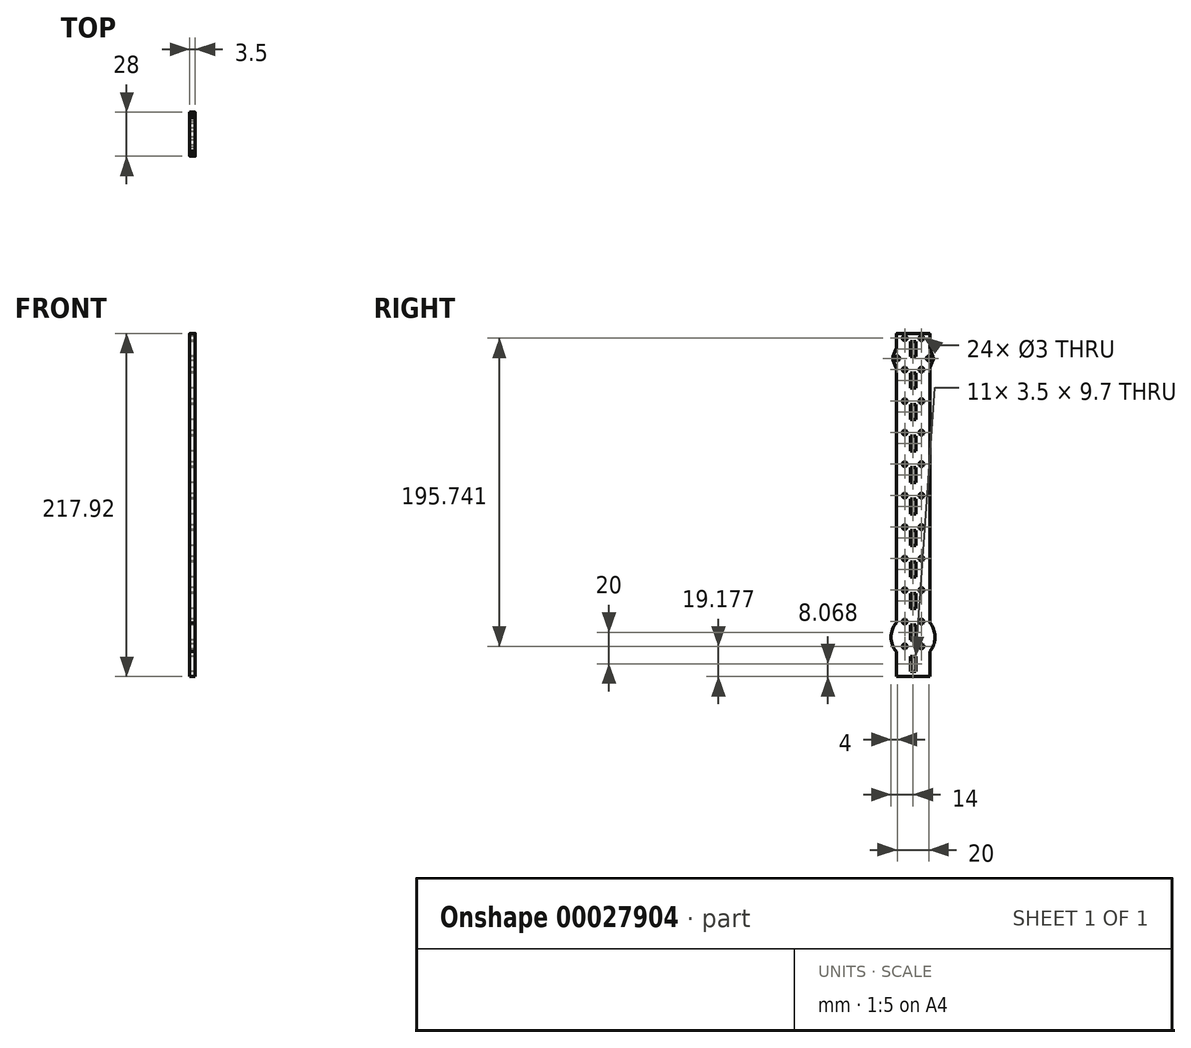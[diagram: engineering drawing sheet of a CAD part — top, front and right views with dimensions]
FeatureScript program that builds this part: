
annotation { "Feature Type Name" : "Feature", "Feature Type Description" : "" }
export const myFeature = defineFeature(function(context is Context, id is Id, definition is map)
    precondition{}
    {
        {
            var Q0;
            Q0=qCreatedBy(makeId("Right.planeOp"),FACE);
            var sketch = newSketch(context, id + "F0", { "sketchPlane" : qUnion([Q0])});
            skLineSegment(sketch, "E0.rect.top", {"start": v(10.14, 107.96) * mm, "end": v(-10.14, 107.96) * mm});
            skLineSegment(sketch, "E0.rect.left", {"start": v(10.64, -107.46) * mm, "end": v(10.64, -94.07) * mm});
            skLineSegment(sketch, "E0.rect.right", {"start": v(-10.64, -107.46) * mm, "end": v(-10.64, -94.07) * mm});
            skPoint(sketch, "E0.rect.middle", {"position": v(0, 0) * mm});
            skLineSegment(sketch, "E1", {"start": v(-10.64, 83.44) * mm, "end": v(10.64, 83.44) * mm, "construction": true});
            skLineSegment(sketch, "E2", {"start": v(10.64, 83.44) * mm, "end": v(0, 107.96) * mm, "construction": true});
            skLineSegment(sketch, "E3", {"start": v(0, 107.96) * mm, "end": v(0, -80.34) * mm, "construction": true});
            skLineSegment(sketch, "E4.rect.bottom", {"start": v(1.75, 93.26) * mm, "end": v(-1.75, 93.26) * mm});
            skLineSegment(sketch, "E4.rect.top", {"start": v(1.75, 102.96) * mm, "end": v(-1.75, 102.96) * mm});
            skLineSegment(sketch, "E4.rect.left", {"start": v(1.75, 93.26) * mm, "end": v(1.75, 102.96) * mm});
            skLineSegment(sketch, "E4.rect.right", {"start": v(-1.75, 93.26) * mm, "end": v(-1.75, 102.96) * mm});
            skPoint(sketch, "E4.rect.middle", {"position": v(0, 98.1) * mm});
            skCircle(sketch, "E5", {"center": v(-5.32, 104.96) * mm, "radius": 1.5 * mm});
            skCircle(sketch, "E6.MirrorC", {"center": v(5.32, 104.96) * mm, "radius": 1.5 * mm});
            skCircle(sketch, "E7.0.1.0", {"center": v(-5.32, 84.96) * mm, "radius": 1.5 * mm});
            skCircle(sketch, "E7.0.1.1", {"center": v(5.32, 84.96) * mm, "radius": 1.5 * mm});
            skLineSegment(sketch, "E7.0.1.2", {"start": v(1.75, 73.26) * mm, "end": v(1.75, 82.96) * mm});
            skLineSegment(sketch, "E7.0.1.3", {"start": v(1.75, 82.96) * mm, "end": v(-1.75, 82.96) * mm});
            skLineSegment(sketch, "E7.0.1.4", {"start": v(-1.75, 73.26) * mm, "end": v(-1.75, 82.96) * mm});
            skLineSegment(sketch, "E7.0.1.5", {"start": v(1.75, 73.26) * mm, "end": v(-1.75, 73.26) * mm});
            skCircle(sketch, "E7.0.2.0", {"center": v(-5.32, 64.96) * mm, "radius": 1.5 * mm});
            skCircle(sketch, "E7.0.2.1", {"center": v(5.32, 64.96) * mm, "radius": 1.5 * mm});
            skLineSegment(sketch, "E7.0.2.2", {"start": v(1.75, 53.26) * mm, "end": v(1.75, 62.96) * mm});
            skLineSegment(sketch, "E7.0.2.3", {"start": v(1.75, 62.96) * mm, "end": v(-1.75, 62.96) * mm});
            skLineSegment(sketch, "E7.0.2.4", {"start": v(-1.75, 53.26) * mm, "end": v(-1.75, 62.96) * mm});
            skLineSegment(sketch, "E7.0.2.5", {"start": v(1.75, 53.26) * mm, "end": v(-1.75, 53.26) * mm});
            skCircle(sketch, "E7.0.3.0", {"center": v(-5.32, 44.96) * mm, "radius": 1.5 * mm});
            skCircle(sketch, "E7.0.3.1", {"center": v(5.32, 44.96) * mm, "radius": 1.5 * mm});
            skLineSegment(sketch, "E7.0.3.2", {"start": v(1.75, 33.26) * mm, "end": v(1.75, 42.96) * mm});
            skLineSegment(sketch, "E7.0.3.3", {"start": v(1.75, 42.96) * mm, "end": v(-1.75, 42.96) * mm});
            skLineSegment(sketch, "E7.0.3.4", {"start": v(-1.75, 33.26) * mm, "end": v(-1.75, 42.96) * mm});
            skLineSegment(sketch, "E7.0.3.5", {"start": v(1.75, 33.26) * mm, "end": v(-1.75, 33.26) * mm});
            skCircle(sketch, "E7.0.4.0", {"center": v(-5.32, 24.96) * mm, "radius": 1.5 * mm});
            skCircle(sketch, "E7.0.4.1", {"center": v(5.32, 24.96) * mm, "radius": 1.5 * mm});
            skLineSegment(sketch, "E7.0.4.2", {"start": v(1.75, 13.26) * mm, "end": v(1.75, 22.96) * mm});
            skLineSegment(sketch, "E7.0.4.3", {"start": v(1.75, 22.96) * mm, "end": v(-1.75, 22.96) * mm});
            skLineSegment(sketch, "E7.0.4.4", {"start": v(-1.75, 13.26) * mm, "end": v(-1.75, 22.96) * mm});
            skLineSegment(sketch, "E7.0.4.5", {"start": v(1.75, 13.26) * mm, "end": v(-1.75, 13.26) * mm});
            skCircle(sketch, "E7.0.5.0", {"center": v(-5.32, 4.96) * mm, "radius": 1.5 * mm});
            skCircle(sketch, "E7.0.5.1", {"center": v(5.32, 4.96) * mm, "radius": 1.5 * mm});
            skLineSegment(sketch, "E7.0.5.2", {"start": v(1.75, -6.74) * mm, "end": v(1.75, 2.96) * mm});
            skLineSegment(sketch, "E7.0.5.3", {"start": v(1.75, 2.96) * mm, "end": v(-1.75, 2.96) * mm});
            skLineSegment(sketch, "E7.0.5.4", {"start": v(-1.75, -6.74) * mm, "end": v(-1.75, 2.96) * mm});
            skLineSegment(sketch, "E7.0.5.5", {"start": v(1.75, -6.74) * mm, "end": v(-1.75, -6.74) * mm});
            skCircle(sketch, "E7.0.6.0", {"center": v(-5.32, -15.04) * mm, "radius": 1.5 * mm});
            skCircle(sketch, "E7.0.6.1", {"center": v(5.32, -15.04) * mm, "radius": 1.5 * mm});
            skLineSegment(sketch, "E7.0.6.2", {"start": v(1.75, -26.74) * mm, "end": v(1.75, -17.04) * mm});
            skLineSegment(sketch, "E7.0.6.3", {"start": v(1.75, -17.04) * mm, "end": v(-1.75, -17.04) * mm});
            skLineSegment(sketch, "E7.0.6.4", {"start": v(-1.75, -26.74) * mm, "end": v(-1.75, -17.04) * mm});
            skLineSegment(sketch, "E7.0.6.5", {"start": v(1.75, -26.74) * mm, "end": v(-1.75, -26.74) * mm});
            skCircle(sketch, "E7.0.7.0", {"center": v(-5.32, -35.04) * mm, "radius": 1.5 * mm});
            skCircle(sketch, "E7.0.7.1", {"center": v(5.32, -35.04) * mm, "radius": 1.5 * mm});
            skLineSegment(sketch, "E7.0.7.2", {"start": v(1.75, -46.74) * mm, "end": v(1.75, -37.04) * mm});
            skLineSegment(sketch, "E7.0.7.3", {"start": v(1.75, -37.04) * mm, "end": v(-1.75, -37.04) * mm});
            skLineSegment(sketch, "E7.0.7.4", {"start": v(-1.75, -46.74) * mm, "end": v(-1.75, -37.04) * mm});
            skLineSegment(sketch, "E7.0.7.5", {"start": v(1.75, -46.74) * mm, "end": v(-1.75, -46.74) * mm});
            skCircle(sketch, "E7.0.8.0", {"center": v(-5.32, -55.04) * mm, "radius": 1.5 * mm});
            skCircle(sketch, "E7.0.8.1", {"center": v(5.32, -55.04) * mm, "radius": 1.5 * mm});
            skLineSegment(sketch, "E7.0.8.2", {"start": v(1.75, -66.74) * mm, "end": v(1.75, -57.04) * mm});
            skLineSegment(sketch, "E7.0.8.3", {"start": v(1.75, -57.04) * mm, "end": v(-1.75, -57.04) * mm});
            skLineSegment(sketch, "E7.0.8.4", {"start": v(-1.75, -66.74) * mm, "end": v(-1.75, -57.04) * mm});
            skLineSegment(sketch, "E7.0.8.5", {"start": v(1.75, -66.74) * mm, "end": v(-1.75, -66.74) * mm});
            skCircle(sketch, "E7.0.9.0", {"center": v(-5.32, -75.04) * mm, "radius": 1.5 * mm});
            skCircle(sketch, "E7.0.9.1", {"center": v(5.32, -75.04) * mm, "radius": 1.5 * mm});
            skLineSegment(sketch, "E7.0.10.2", {"start": v(1.75, -106.74) * mm, "end": v(1.75, -97.04) * mm});
            skLineSegment(sketch, "E7.0.10.3", {"start": v(1.75, -97.04) * mm, "end": v(-1.75, -97.04) * mm});
            skLineSegment(sketch, "E7.0.10.4", {"start": v(-1.75, -106.74) * mm, "end": v(-1.75, -97.04) * mm});
            skLineSegment(sketch, "E7.0.10.5", {"start": v(1.75, -106.74) * mm, "end": v(-1.75, -106.74) * mm});
            skLineSegment(sketch, "E7.direction1", {"start": v(-5.32, 104.96) * mm, "end": v(19.68, 104.96) * mm, "construction": true});
            skLineSegment(sketch, "E7.direction2", {"start": v(-5.32, 104.96) * mm, "end": v(-5.32, 84.96) * mm, "construction": true});
            skArc(sketch, "E8", {"start": v(-10.64, -75.87) * mm, "mid": v(-14, -84.97) * mm, "end": v(-10.64, -94.07) * mm});
            skLineSegment(sketch, "E9.trimOffspring", {"start": v(-10.64, -75.87) * mm, "end": v(-10.64, 107.46) * mm});
            skArc(sketch, "E10.trimOffspring", {"start": v(10.64, -94.07) * mm, "mid": v(14, -84.97) * mm, "end": v(10.64, -75.87) * mm});
            skLineSegment(sketch, "E11.trimOffspring", {"start": v(10.64, -75.87) * mm, "end": v(10.64, 107.46) * mm});
            skPoint(sketch, "E12.orphan", {"position": v(1.75, -77.04) * mm});
            skPoint(sketch, "E13.visualSharp", {"position": v(-10.64, -107.96) * mm});
            skPoint(sketch, "E14.visualSharp", {"position": v(10.64, -107.96) * mm});
            skPoint(sketch, "E15.visualSharp", {"position": v(-10.64, 107.96) * mm});
            skArc(sketch, "E15.filletArc", {"start": v(-10.14, 107.96) * mm, "mid": v(-10.5, 107.81) * mm, "end": v(-10.64, 107.46) * mm});
            skPoint(sketch, "E16.visualSharp", {"position": v(10.64, 107.96) * mm});
            skArc(sketch, "E16.filletArc", {"start": v(10.64, 107.46) * mm, "mid": v(10.5, 107.81) * mm, "end": v(10.14, 107.96) * mm});
            skLineSegment(sketch, "E17.trimOffspring", {"start": v(0, -84.97) * mm, "end": v(0, -107.96) * mm, "construction": true});
            skLineSegment(sketch, "E18.0.1.0", {"start": v(1.75, -86.74) * mm, "end": v(1.75, -77.04) * mm});
            skLineSegment(sketch, "E18.0.1.1", {"start": v(1.75, -86.74) * mm, "end": v(-1.75, -86.74) * mm});
            skLineSegment(sketch, "E18.0.1.2", {"start": v(-1.75, -86.74) * mm, "end": v(-1.75, -77.04) * mm});
            skLineSegment(sketch, "E18.0.1.3", {"start": v(1.75, -77.04) * mm, "end": v(-1.75, -77.04) * mm});
            skLineSegment(sketch, "E18.direction1", {"start": v(1.75, -66.74) * mm, "end": v(26.9, -66.74) * mm, "construction": true});
            skLineSegment(sketch, "E18.direction2", {"start": v(1.75, -66.74) * mm, "end": v(1.75, -86.74) * mm, "construction": true});
            skLineSegment(sketch, "E19", {"start": v(-5.32, -35.04) * mm, "end": v(-5.32, -107.96) * mm, "construction": true});
            skLineSegment(sketch, "E20", {"start": v(5.32, -35.04) * mm, "end": v(5.32, -107.96) * mm, "construction": true});
            skCircle(sketch, "E21", {"center": v(5.32, -90.78) * mm, "radius": 1.5 * mm});
            skCircle(sketch, "E22.MirrorC", {"center": v(-5.32, -90.78) * mm, "radius": 1.5 * mm});
            skCircle(sketch, "E23", {"center": v(-10, 92.13) * mm, "radius": 1.5 * mm});
            skCircle(sketch, "E24.MirrorC", {"center": v(10, 92.13) * mm, "radius": 1.5 * mm});
            skLineSegment(sketch, "E25", {"start": v(16.33, 92.13) * mm, "end": v(-13.22, 92.13) * mm, "construction": true});
            skLineSegment(sketch, "E26", {"start": v(-13.22, 92.13) * mm, "end": v(-10.64, 98.45) * mm});
            skLineSegment(sketch, "E27.MirrorCS", {"start": v(-13.22, 92.13) * mm, "end": v(-10.64, 85.81) * mm});
            skLineSegment(sketch, "E28.MirrorCS", {"start": v(13.22, 92.13) * mm, "end": v(10.64, 98.45) * mm});
            skLineSegment(sketch, "E29.MirrorCS", {"start": v(13.22, 92.13) * mm, "end": v(10.64, 85.81) * mm});
            skLineSegment(sketch, "E30.bottom", {"start": v(0, -107.96) * mm, "end": v(10.64, -107.96) * mm});
            skLineSegment(sketch, "E30.top", {"start": v(-10.64, -109.96) * mm, "end": v(10.64, -109.96) * mm});
            skLineSegment(sketch, "E30.left", {"start": v(-10.64, -107.96) * mm, "end": v(-10.64, -109.96) * mm});
            skLineSegment(sketch, "E30.right", {"start": v(10.64, -107.96) * mm, "end": v(10.64, -109.96) * mm});
            skLineSegment(sketch, "E31", {"start": v(10.64, -107.96) * mm, "end": v(10.64, -107.46) * mm});
            skLineSegment(sketch, "E32", {"start": v(-10.64, -107.96) * mm, "end": v(-10.64, -107.46) * mm});
            skSolve(sketch);
        }
        {
            var Q0;
            Q0 = qSketchRegion(id + "F0", true);
            extrude(context, id + "F1", {"entities" : qUnion([Q0]), "depth" : 3.5 * mm});
        }
        {
            var Q0;
            Q0=makeQuery(id+"F1.opExtrude","SWEPT_EDGE",EDGE,{"disambiguationData":[OSD([sQuery(id+"F0.wireOp",EDGE,"E26"),sQuery(id+"F0.wireOp",EDGE,"E27.MirrorCS")])]});
            var Q1;
            Q1=makeQuery(id+"F1.opExtrude","SWEPT_EDGE",EDGE,{"disambiguationData":[OSD([sQuery(id+"F0.wireOp",EDGE,"b3f7ac1b-f8fb-4887-b317-526ebcccde5e"),sQuery(id+"F0.wireOp",EDGE,"81c05ff1-11e3-4124-91b9-50cd6c8fe2a20.MirrorCS")])]});
            var Q2;
            Q2=makeQuery(id+"F1.opExtrude","SWEPT_EDGE",EDGE,{"disambiguationData":[OSD([sQuery(id+"F0.wireOp",EDGE,"E9.trimOffspring"),sQuery(id+"F0.wireOp",EDGE,"E27.MirrorCS")])]});
            var Q3;
            Q3=makeQuery(id+"F1.opExtrude","SWEPT_EDGE",EDGE,{"disambiguationData":[OSD([sQuery(id+"F0.wireOp",EDGE,"E9.trimOffspring"),sQuery(id+"F0.wireOp",EDGE,"E26")])]});
            var Q4;
            Q4=makeQuery(id+"F1.opExtrude","SWEPT_EDGE",EDGE,{"disambiguationData":[OSD([sQuery(id+"F0.wireOp",EDGE,"E11.trimOffspring"),sQuery(id+"F0.wireOp",EDGE,"b3f7ac1b-f8fb-4887-b317-526ebcccde5e")])]});
            var Q5;
            Q5=makeQuery(id+"F1.opExtrude","SWEPT_EDGE",EDGE,{"disambiguationData":[OSD([sQuery(id+"F0.wireOp",EDGE,"E11.trimOffspring"),sQuery(id+"F0.wireOp",EDGE,"81c05ff1-11e3-4124-91b9-50cd6c8fe2a20.MirrorCS")])]});
            var Q6;
            Q6=makeQuery(id+"F1.opExtrude","SWEPT_EDGE",EDGE,{"disambiguationData":[OSD([sQuery(id+"F0.wireOp",EDGE,"E28.MirrorCS"),sQuery(id+"F0.wireOp",EDGE,"E29.MirrorCS")])]});
            fillet(context, id + "F2", {"entities" : qUnion([Q0, Q1, Q2, Q3, Q4, Q5, Q6]), "radius" : 3 * mm, "tangentPropagation" : true, "allowEdgeOverflow" : false});
        }
    });
